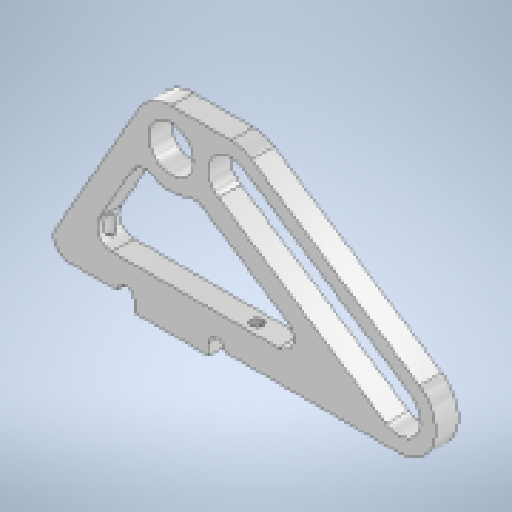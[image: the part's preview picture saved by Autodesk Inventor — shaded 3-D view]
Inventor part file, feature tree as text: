
AUTODESK INVENTOR PART (.ipt)
format: ipt  version: 2025.1 (Build 291241000, 241)  size: 288,768 bytes
history: native  units: mm
features: other x7, reference x7, sketch x6, extrude x5, fillet x3, hole x2
ambient origin geometry x8: Origin, YZ Plane, XZ Plane, XY Plane, X Axis, Y Axis, Z Axis, Center Point
bodies: Body1 (feature_tree)
feature tree (30):
  other  "ソリッド1"
  extrude  "押し出し1"  Depth=6.0mm
  fillet  "フィレット1"  Radius=10.0mm
  extrude  "押し出し6"  Depth=10.0mm
  fillet  "フィレット5"  Radius=1.5mm
  hole  "穴1"  [1 undecoded]
  hole  "穴2"  [1 undecoded]
  sketch  "スケッチ8"
  extrude  "押し出し7"  Depth=10.0mm
  extrude  "押し出し8"  Depth=3.0mm TaperAngle=0.0deg
  fillet  "フィレット6"  Radius=5.0mm
  extrude  "押し出し9"  Depth=5.0mm
  sketch  "スケッチ1"
  sketch  "スケッチ2"
  reference  "参照2"
  sketch  "スケッチ6"
  sketch  "スケッチ7"
  reference  "参照3"
  reference  "参照4"
  reference  "参照5"
  reference  "参照6"
  reference  "参照7"
  reference  "参照8"
  sketch  "スケッチ9"
  other  "<userpath>\Documents\Inventor\Vixen\hizadati_vixen.iam"
  other  "hizadati_vixen.iam"
  other  "kosi_v3_1.5:1"
  other  "<userpath>\Documents\Inventor\Vixen\doutai.iam"
  other  "doutai.iam"
  other  "mount:1"
note: 2 required parameter values undecoded (feature->parameter linkage not recoverable at this tier; creation-order binding heuristic only, values carry confidence <= 0.55)
